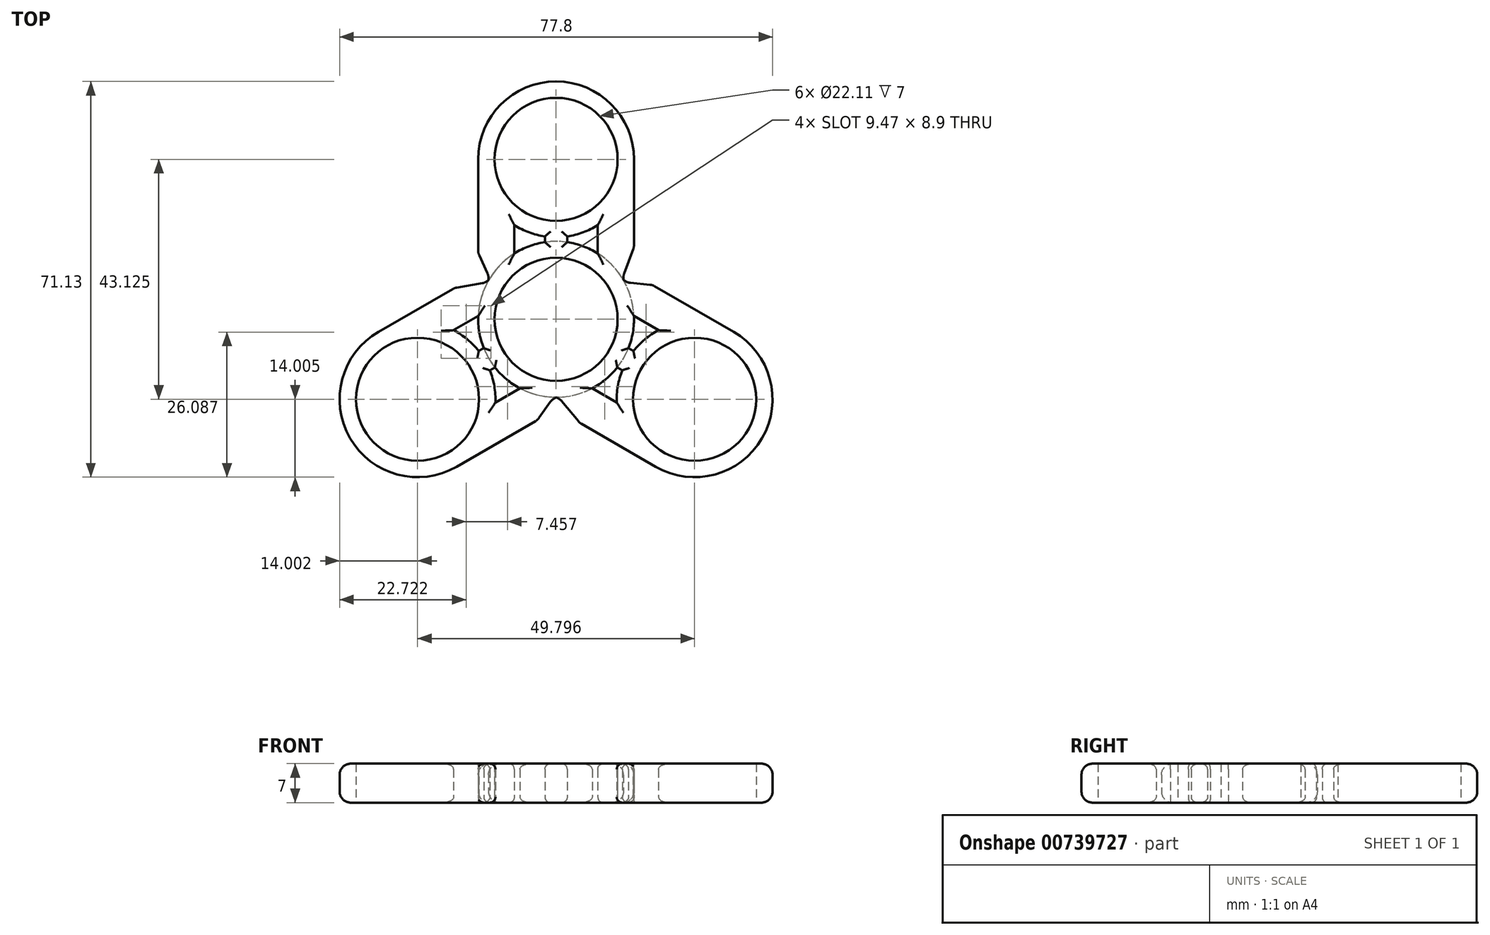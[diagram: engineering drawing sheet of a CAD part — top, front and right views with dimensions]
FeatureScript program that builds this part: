
annotation { "Feature Type Name" : "Feature", "Feature Type Description" : "" }
export const myFeature = defineFeature(function(context is Context, id is Id, definition is map)
    precondition{}
    {
        {
            var Q0;
            Q0=qCreatedBy(makeId("Top.planeOp"),FACE);
            var sketch = newSketch(context, id + "F0", { "sketchPlane" : qUnion([Q0])});
            skLineSegment(sketch, "E0", {"start": v(0, 0) * mm, "end": v(28, 0) * mm});
            skLineSegment(sketch, "E1", {"start": v(28, 0) * mm, "end": v(28, 28.75) * mm});
            skLineSegment(sketch, "E2", {"start": v(28, 28.75) * mm, "end": v(0, 28.75) * mm});
            skLineSegment(sketch, "E3", {"start": v(0, 28.75) * mm, "end": v(0, 0) * mm});
            skCircle(sketch, "E4", {"center": v(14, 28.75) * mm, "radius": 14 * mm});
            skCircle(sketch, "E5", {"center": v(14, 28.75) * mm, "radius": 11.05 * mm});
            skCircle(sketch, "E6", {"center": v(14, 0) * mm, "radius": 14 * mm});
            skCircle(sketch, "E7", {"center": v(14, 0) * mm, "radius": 11.05 * mm});
            skLineSegment(sketch, "E8", {"start": v(6.5, 16.93) * mm, "end": v(6.5, 11.82) * mm});
            skLineSegment(sketch, "E9", {"start": v(21.5, 16.93) * mm, "end": v(21.5, 11.82) * mm});
            skLineSegment(sketch, "E10", {"start": v(0, 11.9) * mm, "end": v(2.09, 7.36) * mm});
            skLineSegment(sketch, "E11", {"start": v(2.09, 7.36) * mm, "end": v(25.91, 7.36) * mm, "construction": true});
            skLineSegment(sketch, "E12", {"start": v(25.91, 7.36) * mm, "end": v(28, 12.98) * mm});
            skLineSegment(sketch, "E13", {"start": v(0, 14.37) * mm, "end": v(28, 14.38) * mm, "construction": true});
            skLineSegment(sketch, "E14.bottom", {"start": v(16, 32.27) * mm, "end": v(12, 32.27) * mm, "construction": true});
            skLineSegment(sketch, "E14.top", {"start": v(16, -3.52) * mm, "end": v(12, -3.52) * mm, "construction": true});
            skLineSegment(sketch, "E14.left", {"start": v(16, 32.27) * mm, "end": v(16, -3.52) * mm});
            skLineSegment(sketch, "E14.right", {"start": v(12, 32.27) * mm, "end": v(12, -3.52) * mm});
            skPoint(sketch, "E14.middle", {"position": v(14, 14.37) * mm});
            skSolve(sketch);
        }
        {
            var Q0;
            {var subQ1=sQuery(id+"F0.wireOp",EDGE,"iIQmwDiW-2rSM-sZxZ-U4c2-H8SH1GVwjlWk");var subQ3=sQuery(id+"F0.wireOp",EDGE,"HfMUf7Gu-QcXs-wyKX-iKiL-St7GXjp5vUj6");var subQ4=makeQuery(id+"F0.imprint","INTERSECT",VERTEX,{"disambiguationData":[OD(0.0)],"derivedFrom":[subQ1,subQ3]});Q0=makeQuery(id+"F0.imprint","IMPRINT",FACE,{"disambiguationData":[TD([[makeQuery(id+"F0.imprint","IMPRINT",EDGE,{"disambiguationData":[TD([[subQ4,-1.0]])],"derivedFrom":subQ3}),-1.0]])]});}
            var Q1;
            {var subQ1=sQuery(id+"F0.wireOp",EDGE,"iIQmwDiW-2rSM-sZxZ-U4c2-H8SH1GVwjlWk");var subQ3=sQuery(id+"F0.wireOp",EDGE,"HfMUf7Gu-QcXs-wyKX-iKiL-St7GXjp5vUj6");var subQ4=makeQuery(id+"F0.imprint","INTERSECT",VERTEX,{"disambiguationData":[OD(0.0)],"derivedFrom":[subQ1,subQ3]});Q1=makeQuery(id+"F0.imprint","IMPRINT",FACE,{"disambiguationData":[TD([[makeQuery(id+"F0.imprint","IMPRINT",EDGE,{"disambiguationData":[TD([[subQ4,1.0]])],"derivedFrom":subQ3}),-1.0]])]});}
            var Q2;
            {var subQ1=sQuery(id+"F0.wireOp",EDGE,"iIQmwDiW-2rSM-sZxZ-U4c2-H8SH1GVwjlWk");var subQ3=sQuery(id+"F0.wireOp",EDGE,"HfMUf7Gu-QcXs-wyKX-iKiL-St7GXjp5vUj6");var subQ4=makeQuery(id+"F0.imprint","INTERSECT",VERTEX,{"disambiguationData":[OD(1.0)],"derivedFrom":[subQ1,subQ3]});Q2=makeQuery(id+"F0.imprint","IMPRINT",FACE,{"disambiguationData":[TD([[makeQuery(id+"F0.imprint","IMPRINT",EDGE,{"disambiguationData":[TD([[subQ4,1.0]])],"derivedFrom":subQ3}),-1.0]])]});}
            var Q3;
            {var subQ0=sQuery(id+"F0.wireOp",EDGE,"pI1Zc2FN-z9bG-iKzO-PqaN-uAXfDf8V6Jii");var subQ1=sQuery(id+"F0.wireOp",EDGE,"1CccQgF1-VPfi-8UMO-eyqF-Bgarba1HzJlT");var subQ2=makeQuery(id+"F0.imprint","INTERSECT",VERTEX,{"derivedFrom":[subQ1,subQ0]});Q3=makeQuery(id+"F0.imprint","IMPRINT",FACE,{"disambiguationData":[TD([[makeQuery(id+"F0.imprint","IMPRINT",EDGE,{"disambiguationData":[TD([[subQ2,-1.0]])],"derivedFrom":subQ1}),1.0]])]});}
            var Q4;
            {var subQ1=sQuery(id+"F0.wireOp",EDGE,"od37IM50-grpF-xB0w-JraC-C9yzX2vZVCVZ");var subQ5=makeQuery(id+"F0.imprint","INTERSECT",VERTEX,{"derivedFrom":[sQuery(id+"F0.wireOp",EDGE,"1CccQgF1-VPfi-8UMO-eyqF-Bgarba1HzJlT"),subQ1]});Q4=makeQuery(id+"F0.imprint","IMPRINT",FACE,{"disambiguationData":[TD([[makeQuery(id+"F0.imprint","IMPRINT",EDGE,{"disambiguationData":[TD([[subQ5,1.0]])],"derivedFrom":subQ1}),1.0]])]});}
            var Q5;
            {var subQ1=sQuery(id+"F0.wireOp",EDGE,"hxwIoEn1-17MV-PHUs-dwTw-XVDV5PBu606Q");var subQ3=sQuery(id+"F0.wireOp",EDGE,"b6EAPOtj-b7LC-Geoj-Rj6s-sGMeLumwryPg");var subQ4=makeQuery(id+"F0.imprint","INTERSECT",VERTEX,{"derivedFrom":[subQ1,subQ3]});Q5=makeQuery(id+"F0.imprint","IMPRINT",FACE,{"disambiguationData":[TD([[makeQuery(id+"F0.imprint","IMPRINT",EDGE,{"disambiguationData":[TD([[subQ4,-1.0]])],"derivedFrom":subQ3}),-1.0]])]});}
            var Q6;
            {var subQ3=sQuery(id+"F0.wireOp",EDGE,"p6FZ0MSm-Ip4u-nYtF-5XC1-SmISDRh16lVO");var subQ5=sQuery(id+"F0.wireOp",EDGE,"b6EAPOtj-b7LC-Geoj-Rj6s-sGMeLumwryPg");var subQ6=makeQuery(id+"F0.imprint","INTERSECT",VERTEX,{"derivedFrom":[subQ5,subQ3]});Q6=makeQuery(id+"F0.imprint","IMPRINT",FACE,{"disambiguationData":[TD([[makeQuery(id+"F0.imprint","IMPRINT",EDGE,{"disambiguationData":[TD([[subQ6,1.0]])],"derivedFrom":subQ5}),-1.0]])]});}
            var Q7;
            {var subQ1=sQuery(id+"F0.wireOp",EDGE,"hxwIoEn1-17MV-PHUs-dwTw-XVDV5PBu606Q");var subQ3=sQuery(id+"F0.wireOp",EDGE,"b6EAPOtj-b7LC-Geoj-Rj6s-sGMeLumwryPg");var subQ4=makeQuery(id+"F0.imprint","INTERSECT",VERTEX,{"derivedFrom":[subQ1,subQ3]});Q7=makeQuery(id+"F0.imprint","IMPRINT",FACE,{"disambiguationData":[TD([[makeQuery(id+"F0.imprint","IMPRINT",EDGE,{"disambiguationData":[TD([[subQ4,1.0]])],"derivedFrom":subQ3}),-1.0]])]});}
            var Q8;
            {var subQ0=sQuery(id+"F0.wireOp",EDGE,"1CccQgF1-VPfi-8UMO-eyqF-Bgarba1HzJlT");var subQ8=makeQuery(id+"F0.imprint","INTERSECT",VERTEX,{"derivedFrom":[sQuery(id+"F0.wireOp",EDGE,"Bk8ssOrG-JtuW-JQn9-LGAU-KgTtz2KieB6C"),subQ0]});Q8=makeQuery(id+"F0.imprint","IMPRINT",FACE,{"disambiguationData":[TD([[makeQuery(id+"F0.imprint","IMPRINT",EDGE,{"disambiguationData":[TD([[subQ8,1.0]])],"derivedFrom":subQ0}),1.0]])]});}
            var Q9;
            {var subQ1=sQuery(id+"F0.wireOp",EDGE,"E2");var subQ3=sQuery(id+"F0.wireOp",EDGE,"E5");var subQ4=makeQuery(id+"F0.imprint","INTERSECT",VERTEX,{"disambiguationData":[OD(0.0)],"derivedFrom":[subQ1,subQ3]});Q9=makeQuery(id+"F0.imprint","IMPRINT",FACE,{"disambiguationData":[TD([[makeQuery(id+"F0.imprint","IMPRINT",EDGE,{"disambiguationData":[TD([[subQ4,-1.0]])],"derivedFrom":subQ3}),-1.0]])]});}
            var Q10;
            {var subQ0=sQuery(id+"F0.wireOp",EDGE,"E4");var subQ1=makeQuery(id+"F0.imprint","INTERSECT",VERTEX,{"derivedFrom":[subQ0,sQuery(id+"F0.wireOp",EDGE,"E8")]});Q10=makeQuery(id+"F0.imprint","IMPRINT",FACE,{"disambiguationData":[TD([[makeQuery(id+"F0.imprint","IMPRINT",EDGE,{"disambiguationData":[TD([[subQ1,-1.0]])],"derivedFrom":subQ0}),1.0]])]});}
            var Q11;
            {var subQ0=sQuery(id+"F0.wireOp",EDGE,"E6");var subQ6=makeQuery(id+"F0.imprint","INTERSECT",VERTEX,{"derivedFrom":[subQ0,sQuery(id+"F0.wireOp",EDGE,"E8")]});Q11=makeQuery(id+"F0.imprint","IMPRINT",FACE,{"disambiguationData":[TD([[makeQuery(id+"F0.imprint","IMPRINT",EDGE,{"disambiguationData":[TD([[subQ6,1.0]])],"derivedFrom":subQ0}),1.0]])]});}
            var Q12;
            {var subQ1=sQuery(id+"F0.wireOp",EDGE,"E0");var subQ3=sQuery(id+"F0.wireOp",EDGE,"E7");var subQ4=makeQuery(id+"F0.imprint","INTERSECT",VERTEX,{"disambiguationData":[OD(0.0)],"derivedFrom":[subQ1,subQ3]});Q12=makeQuery(id+"F0.imprint","IMPRINT",FACE,{"disambiguationData":[TD([[makeQuery(id+"F0.imprint","IMPRINT",EDGE,{"disambiguationData":[TD([[subQ4,-1.0]])],"derivedFrom":subQ3}),-1.0]])]});}
            var Q13;
            {var subQ0=sQuery(id+"F0.wireOp",EDGE,"E8");Q13=makeQuery(id+"F0.imprint","IMPRINT",FACE,{"disambiguationData":[TD([[makeQuery(id+"F0.imprint","IMPRINT",EDGE,{"derivedFrom":subQ0}),-1.0]])]});}
            var Q14;
            {var subQ0=sQuery(id+"F0.wireOp",EDGE,"E9");Q14=makeQuery(id+"F0.imprint","IMPRINT",FACE,{"disambiguationData":[TD([[makeQuery(id+"F0.imprint","IMPRINT",EDGE,{"derivedFrom":subQ0}),1.0]])]});}
            var Q15;
            {var subQ0=sQuery(id+"F0.wireOp",EDGE,"E14.right");var subQ1=sQuery(id+"F0.wireOp",EDGE,"E4");var subQ2=makeQuery(id+"F0.imprint","INTERSECT",VERTEX,{"derivedFrom":[subQ1,subQ0]});Q15=makeQuery(id+"F0.imprint","IMPRINT",FACE,{"disambiguationData":[TD([[makeQuery(id+"F0.imprint","IMPRINT",EDGE,{"disambiguationData":[TD([[subQ2,-1.0]])],"derivedFrom":subQ1}),1.0]])]});}
            var Q16;
            {var subQ0=sQuery(id+"F0.wireOp",EDGE,"E4");var subQ3=makeQuery(id+"F0.imprint","INTERSECT",VERTEX,{"derivedFrom":[subQ0,sQuery(id+"F0.wireOp",EDGE,"E9")]});Q16=makeQuery(id+"F0.imprint","IMPRINT",FACE,{"disambiguationData":[TD([[makeQuery(id+"F0.imprint","IMPRINT",EDGE,{"disambiguationData":[TD([[subQ3,1.0]])],"derivedFrom":subQ0}),1.0]])]});}
            var Q17;
            {var subQ0=sQuery(id+"F0.wireOp",EDGE,"E14.right");var subQ1=sQuery(id+"F0.wireOp",EDGE,"E4");var subQ2=makeQuery(id+"F0.imprint","INTERSECT",VERTEX,{"derivedFrom":[subQ1,subQ0]});Q17=makeQuery(id+"F0.imprint","IMPRINT",FACE,{"disambiguationData":[TD([[makeQuery(id+"F0.imprint","IMPRINT",EDGE,{"disambiguationData":[TD([[subQ2,-1.0]])],"derivedFrom":subQ1}),-1.0]])]});}
            var Q18;
            {var subQ0=sQuery(id+"F0.wireOp",EDGE,"E14.left");var subQ1=sQuery(id+"F0.wireOp",EDGE,"E6");var subQ2=makeQuery(id+"F0.imprint","INTERSECT",VERTEX,{"derivedFrom":[subQ1,subQ0]});Q18=makeQuery(id+"F0.imprint","IMPRINT",FACE,{"disambiguationData":[TD([[makeQuery(id+"F0.imprint","IMPRINT",EDGE,{"disambiguationData":[TD([[subQ2,-1.0]])],"derivedFrom":subQ1}),1.0]])]});}
            var Q19;
            {var subQ0=sQuery(id+"F0.wireOp",EDGE,"E6");var subQ1=makeQuery(id+"F0.imprint","INTERSECT",VERTEX,{"derivedFrom":[subQ0,sQuery(id+"F0.wireOp",EDGE,"E9")]});Q19=makeQuery(id+"F0.imprint","IMPRINT",FACE,{"disambiguationData":[TD([[makeQuery(id+"F0.imprint","IMPRINT",EDGE,{"disambiguationData":[TD([[subQ1,1.0]])],"derivedFrom":subQ0}),1.0]])]});}
            extrude(context, id + "F1", {"entities" : qUnion([Q0, Q1, Q2, Q3, Q4, Q5, Q6, Q7, Q8, Q9, Q10, Q11, Q12, Q13, Q14, Q15, Q16, Q17, Q18, Q19]), "depth" : 7 * mm, "offsetDistance" : 25 * mm});
        }
        {
            var Q0;
            Q0=makeQuery(id+"F1.opExtrude","CAP_EDGE",EDGE,{"disambiguationData":[OSD([sQuery(id+"F0.wireOp",EDGE,"E3")])],"isStart":false});
            var Q1;
            {var subQ0=sQuery(id+"F0.wireOp",EDGE,"E4");var subQ1=sQuery(id+"F0.wireOp",EDGE,"E2");Q1=makeQuery(id+"F1.opExtrude","CAP_EDGE",EDGE,{"disambiguationData":[OSD([subQ0]),TDD([makeQuery(id+"F0.imprint","IMPRINT",EDGE,{"disambiguationData":[TD([[makeQuery(id+"F0.imprint","INTERSECT",VERTEX,{"derivedFrom":[sQuery(id+"F0.wireOp",EDGE,"E1"),subQ1,subQ0]}),-1.0]])],"derivedFrom":subQ0})])],"isStart":false});}
            var Q2;
            {var subQ0=sQuery(id+"F0.wireOp",EDGE,"E6");var subQ1=sQuery(id+"F0.wireOp",EDGE,"E0");Q2=makeQuery(id+"F1.opExtrude","CAP_EDGE",EDGE,{"disambiguationData":[OSD([subQ0]),TDD([makeQuery(id+"F0.imprint","IMPRINT",EDGE,{"disambiguationData":[TD([[makeQuery(id+"F0.imprint","INTERSECT",VERTEX,{"derivedFrom":[subQ1,sQuery(id+"F0.wireOp",EDGE,"E3"),subQ0]}),-1.0]])],"derivedFrom":subQ0})])],"isStart":false});}
            var Q3;
            Q3=makeQuery(id+"F1.opExtrude","CAP_EDGE",EDGE,{"disambiguationData":[OSD([sQuery(id+"F0.wireOp",EDGE,"E1")])],"isStart":false});
            var Q4;
            Q4=makeQuery(id+"F1.opExtrude","CAP_EDGE",EDGE,{"disambiguationData":[OSD([sQuery(id+"F0.wireOp",EDGE,"E1")])],"isStart":true});
            var Q5;
            {var subQ0=sQuery(id+"F0.wireOp",EDGE,"E6");var subQ1=sQuery(id+"F0.wireOp",EDGE,"E0");Q5=makeQuery(id+"F1.opExtrude","CAP_EDGE",EDGE,{"disambiguationData":[OSD([subQ0]),TDD([makeQuery(id+"F0.imprint","IMPRINT",EDGE,{"disambiguationData":[TD([[makeQuery(id+"F0.imprint","INTERSECT",VERTEX,{"derivedFrom":[subQ1,sQuery(id+"F0.wireOp",EDGE,"E3"),subQ0]}),-1.0]])],"derivedFrom":subQ0})])],"isStart":true});}
            var Q6;
            {var subQ0=sQuery(id+"F0.wireOp",EDGE,"E4");var subQ1=sQuery(id+"F0.wireOp",EDGE,"E2");Q6=makeQuery(id+"F1.opExtrude","CAP_EDGE",EDGE,{"disambiguationData":[OSD([subQ0]),TDD([makeQuery(id+"F0.imprint","IMPRINT",EDGE,{"disambiguationData":[TD([[makeQuery(id+"F0.imprint","INTERSECT",VERTEX,{"derivedFrom":[sQuery(id+"F0.wireOp",EDGE,"E1"),subQ1,subQ0]}),-1.0]])],"derivedFrom":subQ0})])],"isStart":true});}
            var Q7;
            Q7=makeQuery(id+"F1.opExtrude","CAP_EDGE",EDGE,{"disambiguationData":[OSD([sQuery(id+"F0.wireOp",EDGE,"E3")])],"isStart":true});
            var Q8;
            Q8=makeQuery(id+"F1.opExtrude","SWEPT_FACE",FACE,{"disambiguationData":[OSD([sQuery(id+"F0.wireOp",EDGE,"E12")])]});
            var Q9;
            Q9=makeQuery(id+"F1.opExtrude","SWEPT_FACE",FACE,{"disambiguationData":[OSD([sQuery(id+"F0.wireOp",EDGE,"E10")])]});
            fillet(context, id + "F2", {"entities" : qUnion([Q0, Q1, Q2, Q3, Q4, Q5, Q6, Q7, Q8, Q9]), "radius" : 2 * mm, "tangentPropagation" : true, "allowEdgeOverflow" : false});
        }
        {
            var Q0;
            {var subQ0=sQuery(id+"F0.wireOp",EDGE,"E4");Q0=makeQuery(id+"F1.opExtrude","CAP_EDGE",EDGE,{"disambiguationData":[OSD([subQ0]),TDD([makeQuery(id+"F0.imprint","IMPRINT",EDGE,{"disambiguationData":[TD([[makeQuery(id+"F0.imprint","INTERSECT",VERTEX,{"derivedFrom":[subQ0,sQuery(id+"F0.wireOp",EDGE,"E8")]}),-1.0]])],"derivedFrom":subQ0})])],"isStart":false});}
            var Q1;
            Q1=makeQuery(id+"F1.opExtrude","CAP_EDGE",EDGE,{"disambiguationData":[OSD([sQuery(id+"F0.wireOp",EDGE,"E8")])],"isStart":false});
            var Q2;
            Q2=makeQuery(id+"F1.opExtrude","CAP_EDGE",EDGE,{"disambiguationData":[OSD([sQuery(id+"F0.wireOp",EDGE,"E9")])],"isStart":false});
            var Q3;
            {var subQ0=sQuery(id+"F0.wireOp",EDGE,"E6");Q3=makeQuery(id+"F1.opExtrude","CAP_EDGE",EDGE,{"disambiguationData":[OSD([subQ0]),TDD([makeQuery(id+"F0.imprint","IMPRINT",EDGE,{"disambiguationData":[TD([[makeQuery(id+"F0.imprint","INTERSECT",VERTEX,{"derivedFrom":[subQ0,sQuery(id+"F0.wireOp",EDGE,"E8")]}),1.0]])],"derivedFrom":subQ0})])],"isStart":false});}
            var Q4;
            {var subQ0=sQuery(id+"F0.wireOp",EDGE,"E6");Q4=makeQuery(id+"F1.opExtrude","CAP_EDGE",EDGE,{"disambiguationData":[OSD([subQ0]),TDD([makeQuery(id+"F0.imprint","IMPRINT",EDGE,{"disambiguationData":[TD([[makeQuery(id+"F0.imprint","INTERSECT",VERTEX,{"derivedFrom":[subQ0,sQuery(id+"F0.wireOp",EDGE,"E8")]}),1.0]])],"derivedFrom":subQ0})])],"isStart":true});}
            var Q5;
            {var subQ0=sQuery(id+"F0.wireOp",EDGE,"E4");Q5=makeQuery(id+"F1.opExtrude","CAP_EDGE",EDGE,{"disambiguationData":[OSD([subQ0]),TDD([makeQuery(id+"F0.imprint","IMPRINT",EDGE,{"disambiguationData":[TD([[makeQuery(id+"F0.imprint","INTERSECT",VERTEX,{"derivedFrom":[subQ0,sQuery(id+"F0.wireOp",EDGE,"E8")]}),-1.0]])],"derivedFrom":subQ0})])],"isStart":true});}
            var Q6;
            Q6=makeQuery(id+"F1.opExtrude","CAP_EDGE",EDGE,{"disambiguationData":[OSD([sQuery(id+"F0.wireOp",EDGE,"E9")])],"isStart":true});
            var Q7;
            Q7=makeQuery(id+"F1.opExtrude","CAP_EDGE",EDGE,{"disambiguationData":[OSD([sQuery(id+"F0.wireOp",EDGE,"E8")])],"isStart":true});
            var Q8;
            Q8=makeQuery(id+"F1.opExtrude","CAP_EDGE",EDGE,{"disambiguationData":[OSD([sQuery(id+"F0.wireOp",EDGE,"E14.right")])],"isStart":false});
            var Q9;
            Q9=makeQuery(id+"F1.opExtrude","CAP_EDGE",EDGE,{"disambiguationData":[OSD([sQuery(id+"F0.wireOp",EDGE,"E14.left")])],"isStart":false});
            var Q10;
            {var subQ0=sQuery(id+"F0.wireOp",EDGE,"E4");Q10=makeQuery(id+"F1.opExtrude","CAP_EDGE",EDGE,{"disambiguationData":[OSD([subQ0]),TDD([makeQuery(id+"F0.imprint","IMPRINT",EDGE,{"disambiguationData":[TD([[makeQuery(id+"F0.imprint","INTERSECT",VERTEX,{"derivedFrom":[subQ0,sQuery(id+"F0.wireOp",EDGE,"E9")]}),1.0]])],"derivedFrom":subQ0})])],"isStart":false});}
            var Q11;
            {var subQ0=sQuery(id+"F0.wireOp",EDGE,"E6");Q11=makeQuery(id+"F1.opExtrude","CAP_EDGE",EDGE,{"disambiguationData":[OSD([subQ0]),TDD([makeQuery(id+"F0.imprint","IMPRINT",EDGE,{"disambiguationData":[TD([[makeQuery(id+"F0.imprint","INTERSECT",VERTEX,{"derivedFrom":[subQ0,sQuery(id+"F0.wireOp",EDGE,"E9")]}),-1.0]])],"derivedFrom":subQ0})])],"isStart":false});}
            var Q12;
            Q12=makeQuery(id+"F1.opExtrude","CAP_EDGE",EDGE,{"disambiguationData":[OSD([sQuery(id+"F0.wireOp",EDGE,"E14.right")])],"isStart":true});
            var Q13;
            {var subQ0=sQuery(id+"F0.wireOp",EDGE,"E6");Q13=makeQuery(id+"F1.opExtrude","CAP_EDGE",EDGE,{"disambiguationData":[OSD([subQ0]),TDD([makeQuery(id+"F0.imprint","IMPRINT",EDGE,{"disambiguationData":[TD([[makeQuery(id+"F0.imprint","INTERSECT",VERTEX,{"derivedFrom":[subQ0,sQuery(id+"F0.wireOp",EDGE,"E9")]}),-1.0]])],"derivedFrom":subQ0})])],"isStart":true});}
            var Q14;
            {var subQ0=sQuery(id+"F0.wireOp",EDGE,"E4");Q14=makeQuery(id+"F1.opExtrude","CAP_EDGE",EDGE,{"disambiguationData":[OSD([subQ0]),TDD([makeQuery(id+"F0.imprint","IMPRINT",EDGE,{"disambiguationData":[TD([[makeQuery(id+"F0.imprint","INTERSECT",VERTEX,{"derivedFrom":[subQ0,sQuery(id+"F0.wireOp",EDGE,"E9")]}),1.0]])],"derivedFrom":subQ0})])],"isStart":true});}
            var Q15;
            Q15=makeQuery(id+"F1.opExtrude","CAP_EDGE",EDGE,{"disambiguationData":[OSD([sQuery(id+"F0.wireOp",EDGE,"E14.left")])],"isStart":true});
            fillet(context, id + "F3", {"entities" : qUnion([Q0, Q1, Q2, Q3, Q4, Q5, Q6, Q7, Q8, Q9, Q10, Q11, Q12, Q13, Q14, Q15]), "radius" : 1 * mm, "tangentPropagation" : true, "allowEdgeOverflow" : false});
        }
        {
            var Q0;
            Q0=makeQuery(id+"F1.opExtrude","SWEPT_BODY",BODY,{"disambiguationData":[OSD([sQuery(id+"F0.wireOp",EDGE,"E1"),sQuery(id+"F0.wireOp",EDGE,"E3"),sQuery(id+"F0.wireOp",EDGE,"E4"),sQuery(id+"F0.wireOp",EDGE,"E5"),sQuery(id+"F0.wireOp",EDGE,"E6"),sQuery(id+"F0.wireOp",EDGE,"E7"),sQuery(id+"F0.wireOp",EDGE,"E8"),sQuery(id+"F0.wireOp",EDGE,"E9")])]});
            var Q1;
            {var subQ0=sQuery(id+"F0.wireOp",EDGE,"E6");var subQ1=sQuery(id+"F0.wireOp",EDGE,"E0");Q1=makeQuery(id+"F1.opExtrude","SWEPT_FACE",FACE,{"disambiguationData":[OSD([subQ0]),TDD([makeQuery(id+"F0.imprint","IMPRINT",EDGE,{"disambiguationData":[TD([[makeQuery(id+"F0.imprint","INTERSECT",VERTEX,{"derivedFrom":[subQ1,sQuery(id+"F0.wireOp",EDGE,"E3"),subQ0]}),-1.0]])],"derivedFrom":subQ0})])]});}
            circularPattern(context, id + "F4", {"entities" : qUnion([Q0]), "axis" : qUnion([Q1]), "angle" : 360 * degree, "instanceCount" : 3, "equalSpace" : true});
        }
    });
